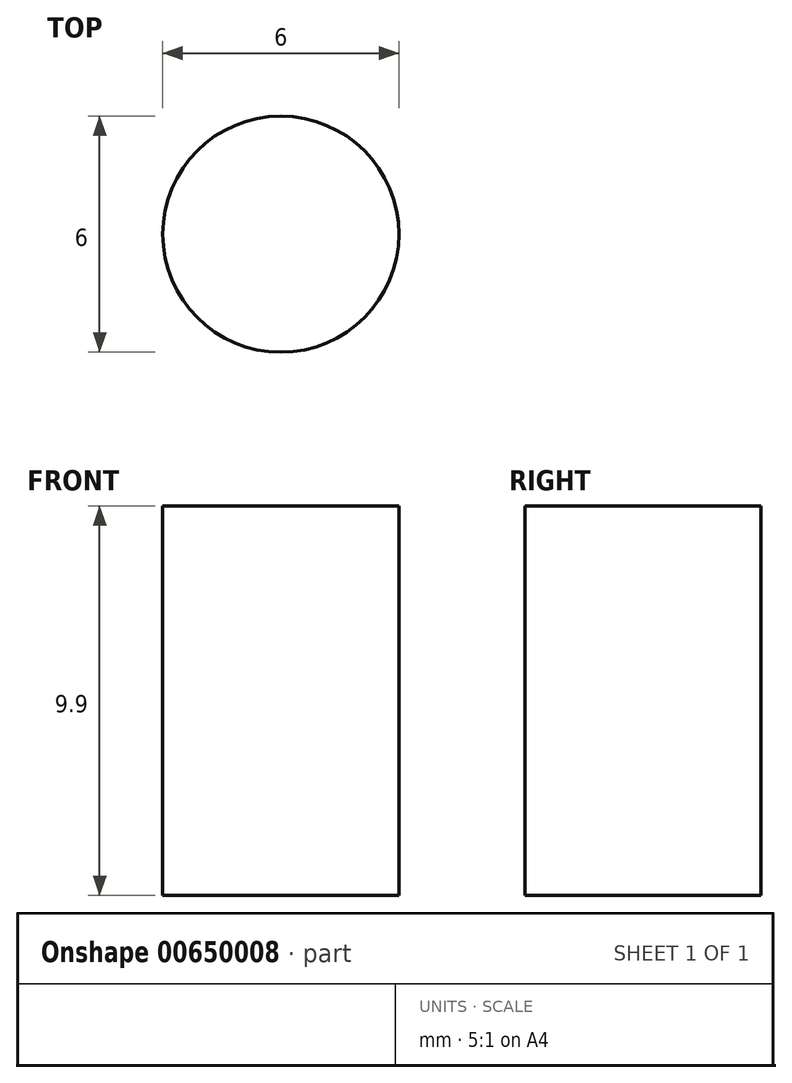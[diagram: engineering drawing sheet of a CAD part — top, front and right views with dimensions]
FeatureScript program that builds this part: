
annotation { "Feature Type Name" : "Feature", "Feature Type Description" : "" }
export const myFeature = defineFeature(function(context is Context, id is Id, definition is map)
    precondition{}
    {
        {
            assignVariable(context, id + "F0", {"name" : "diode_height", "anyValue" : 9.9});
        }
        {
            var Q0;
            Q0=qCreatedBy(makeId("Top.planeOp"),FACE);
            var sketch = newSketch(context, id + "F1", { "sketchPlane" : qUnion([Q0])});
            skCircle(sketch, "E0", {"center": v(0, 0) * mm, "radius": 3 * mm});
            skSolve(sketch);
        }
        {
            var Q0;
            Q0=makeQuery(id+"F1.imprint","IMPRINT",FACE,{"disambiguationData":[TD([[makeQuery(id+"F1.imprint","IMPRINT",EDGE,{"derivedFrom":sQuery(id+"F1.wireOp",EDGE,"E0")}),1.0]])]});
            extrude(context, id + "F2", {"entities" : qUnion([Q0]), "depth" : (getVariable(context, 'diode_height')) * mm, "offsetDistance" : 25 * mm});
        }
    });
